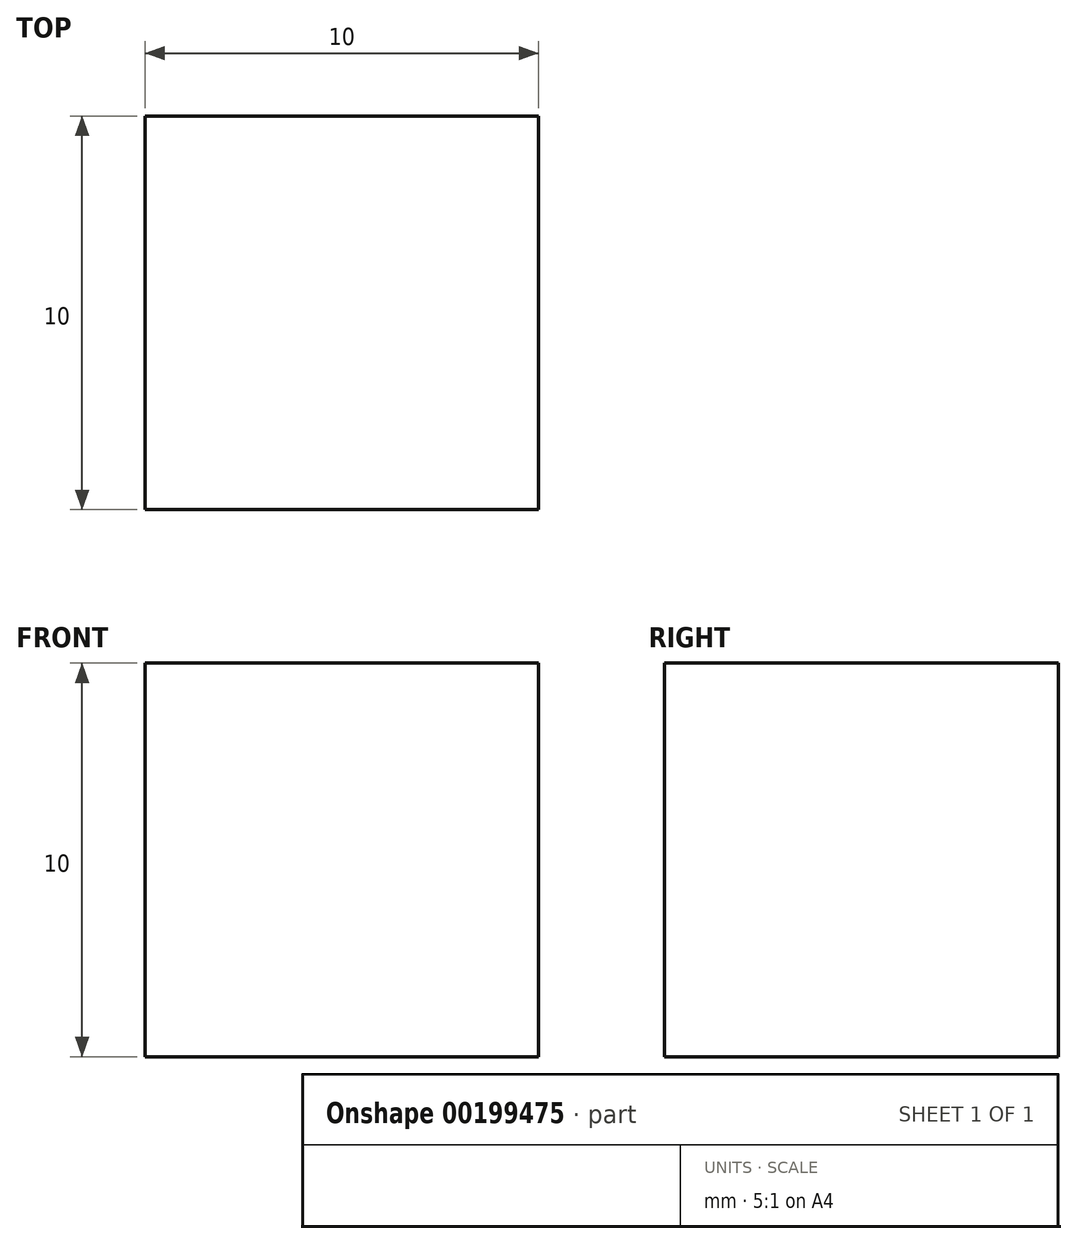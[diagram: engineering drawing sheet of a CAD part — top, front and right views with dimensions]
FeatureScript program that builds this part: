
annotation { "Feature Type Name" : "Feature", "Feature Type Description" : "" }
export const myFeature = defineFeature(function(context is Context, id is Id, definition is map)
    precondition{}
    {
        {
            var Q0;
            Q0=qCreatedBy(makeId("Top.planeOp"),FACE);
            var sketch = newSketch(context, id + "F0", { "sketchPlane" : qUnion([Q0])});
            skLineSegment(sketch, "E0.bottom", {"start": v(5, 5) * mm, "end": v(-5, 5) * mm});
            skLineSegment(sketch, "E0.top", {"start": v(5, -5) * mm, "end": v(-5, -5) * mm});
            skLineSegment(sketch, "E0.left", {"start": v(5, 5) * mm, "end": v(5, -5) * mm});
            skLineSegment(sketch, "E0.right", {"start": v(-5, 5) * mm, "end": v(-5, -5) * mm});
            skPoint(sketch, "E0.middle", {"position": v(0, 0) * mm});
            skSolve(sketch);
        }
        {
            var Q0;
            Q0=makeQuery(id+"F0.imprint","IMPRINT",FACE,{"disambiguationData":[TD([[makeQuery(id+"F0.imprint","IMPRINT",EDGE,{"derivedFrom":sQuery(id+"F0.wireOp",EDGE,"E0.bottom")}),1.0]])]});
            extrude(context, id + "F1", {"entities" : qUnion([Q0]), "depth" : 10 * mm});
        }
    });
